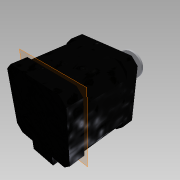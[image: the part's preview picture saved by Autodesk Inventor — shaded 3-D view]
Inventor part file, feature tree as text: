
AUTODESK INVENTOR PART (.ipt)
format: ipt  version: 2014 (Build 180170000, 170)  size: 189,952 bytes
history: native  units: mm
features: extrude x9, sketch x9, chamfer x1, plane x1, pattern_circular x1, projected_geometry x1
ambient origin geometry x8: Origin, YZ Plane, XZ Plane, XY Plane, X Axis, Y Axis, Z Axis, Center Point
bodies: Solid1 (feature_tree), Solid2 (feature_tree)
feature tree (22):
  extrude  "Extrusion1"  Depth=42.0mm
  extrude  "Extrusion2"  Depth=45.0mm
  extrude  "Extrusion3"  Depth=2.0mm
  chamfer  "Chamfer1"  Distance=10.0mm
  extrude  "Extrusion4"  Depth=5.0mm
  plane  "Work Plane1"
  extrude  "Extrusion5"  Depth=21.0mm TaperAngle=0.0deg
  pattern_circular  "Circular Pattern1"  [2 undecoded]
  extrude  "Extrusion6"  Depth=28.0mm TaperAngle=0.0deg
  extrude  "Extrusion7"  Depth=6.0mm TaperAngle=360.0deg
  extrude  "Extrusion8"  Depth=18.0mm
  extrude  "Extrusion9"  Depth=1.5mm TaperAngle=0.0deg
  sketch  "Sketch1"  dims[d0=42.0mm d1=42.0mm]
  sketch  "Sketch3"  dims[d2=45.0mm d3=0.0mm d4=20.0mm]
  sketch  "Sketch4"  dims[d5=2.0mm d6=0.0mm d7=31.0mm]
  sketch  "Sketch5"  dims[d8=31.0mm]
  sketch  "Sketch6"  dims[d9=3.0mm]
  projected_geometry  "Projected Loop1"
  sketch  "Sketch7"  dims[d10=3.0mm]
  sketch  "Sketch8"  dims[d11=3.0mm]
  sketch  "Sketch9"  dims[d12=3.0mm d13=10.0mm d14=0.0mm]
  sketch  "Sketch10"  dims[d15=4.0mm d16=2.0mm d17=45.0deg d18=5.0mm d19=21.0mm d20=0.0mm d21=-9.2mm d22=28.0mm d23=0.0mm d24=40.0mm d25=360.0deg d27=18.0mm d28=1.5mm d29=0.0mm d30=11.0mm d31=7.5mm d32=0.0mm d33=18.0mm d34=9.0mm d35=0.0mm d36=16.0mm d37=8.0mm d38=6.0mm d39=0.0mm]
note: 2 required parameter values undecoded (feature->parameter linkage not recoverable at this tier; creation-order binding heuristic only, values carry confidence <= 0.55)
